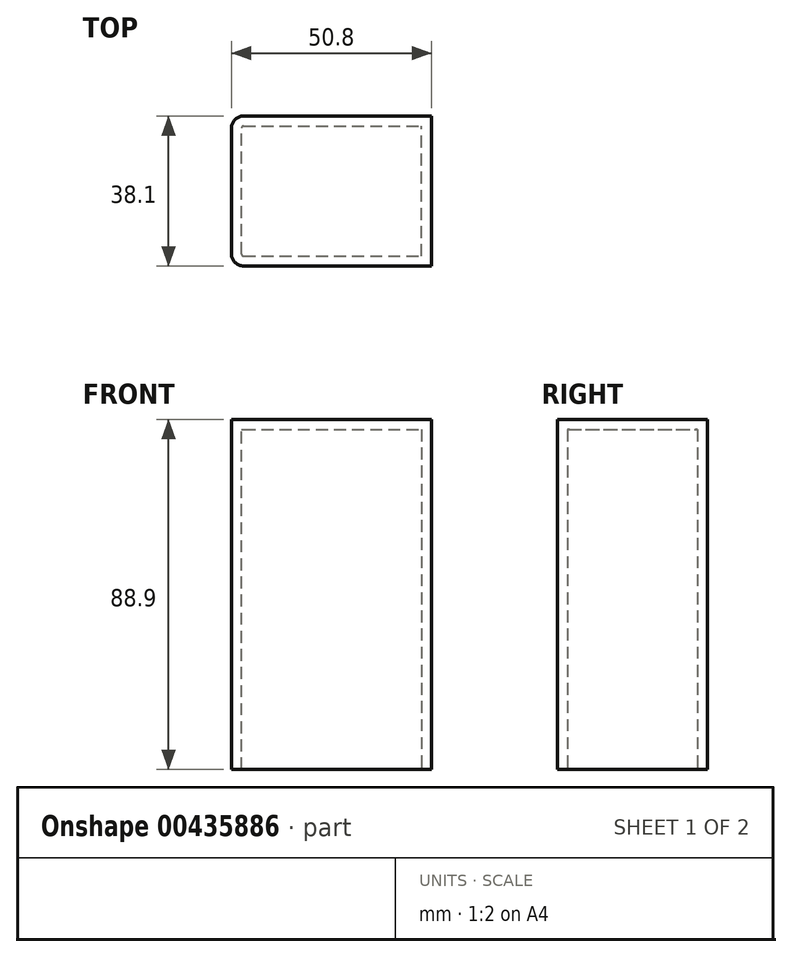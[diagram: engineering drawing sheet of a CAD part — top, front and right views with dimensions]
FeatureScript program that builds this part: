
annotation { "Feature Type Name" : "Feature", "Feature Type Description" : "" }
export const myFeature = defineFeature(function(context is Context, id is Id, definition is map)
    precondition{}
    {
        {
            var Q0;
            Q0=qCreatedBy(makeId("Top.planeOp"),FACE);
            var sketch = newSketch(context, id + "F0", { "sketchPlane" : qUnion([Q0])});
            skLineSegment(sketch, "E0.bottom", {"start": v(0, 0) * mm, "end": v(50.8, 0) * mm});
            skLineSegment(sketch, "E0.top", {"start": v(0, 38.1) * mm, "end": v(50.8, 38.1) * mm});
            skLineSegment(sketch, "E0.left", {"start": v(0, 0) * mm, "end": v(0, 38.1) * mm});
            skLineSegment(sketch, "E0.right", {"start": v(50.8, 0) * mm, "end": v(50.8, 38.1) * mm});
            skSolve(sketch);
        }
        {
            var Q0;
            Q0 = qSketchRegion(id + "F0", true);
            extrude(context, id + "F1", {"entities" : qUnion([Q0]), "depth" : 88.9 * mm});
        }
        {
            var Q0;
            Q0=makeQuery(id+"F1.opExtrude","SWEPT_EDGE",EDGE,{"disambiguationData":[OSD([sQuery(id+"F0.wireOp",EDGE,"E0.bottom"),sQuery(id+"F0.wireOp",EDGE,"E0.left")])]});
            var Q1;
            Q1=makeQuery(id+"F1.opExtrude","SWEPT_EDGE",EDGE,{"disambiguationData":[OSD([sQuery(id+"F0.wireOp",EDGE,"E0.top"),sQuery(id+"F0.wireOp",EDGE,"E0.left")])]});
            fillet(context, id + "F2", {"entities" : qUnion([Q0, Q1]), "radius" : 3.05 * mm, "tangentPropagation" : true, "allowEdgeOverflow" : false});
        }
        {
            var Q0;
            Q0=makeQuery(id+"F1.opExtrude","CAP_FACE",FACE,{"disambiguationData":[OSD([sQuery(id+"F0.wireOp",EDGE,"E0.bottom"),sQuery(id+"F0.wireOp",EDGE,"E0.top"),sQuery(id+"F0.wireOp",EDGE,"E0.left"),sQuery(id+"F0.wireOp",EDGE,"E0.right")])],"isStart":true});
            shell(context, id + "F3", {"entities" : qUnion([Q0]), "thickness" : 2.54 * mm});
        }
    });
